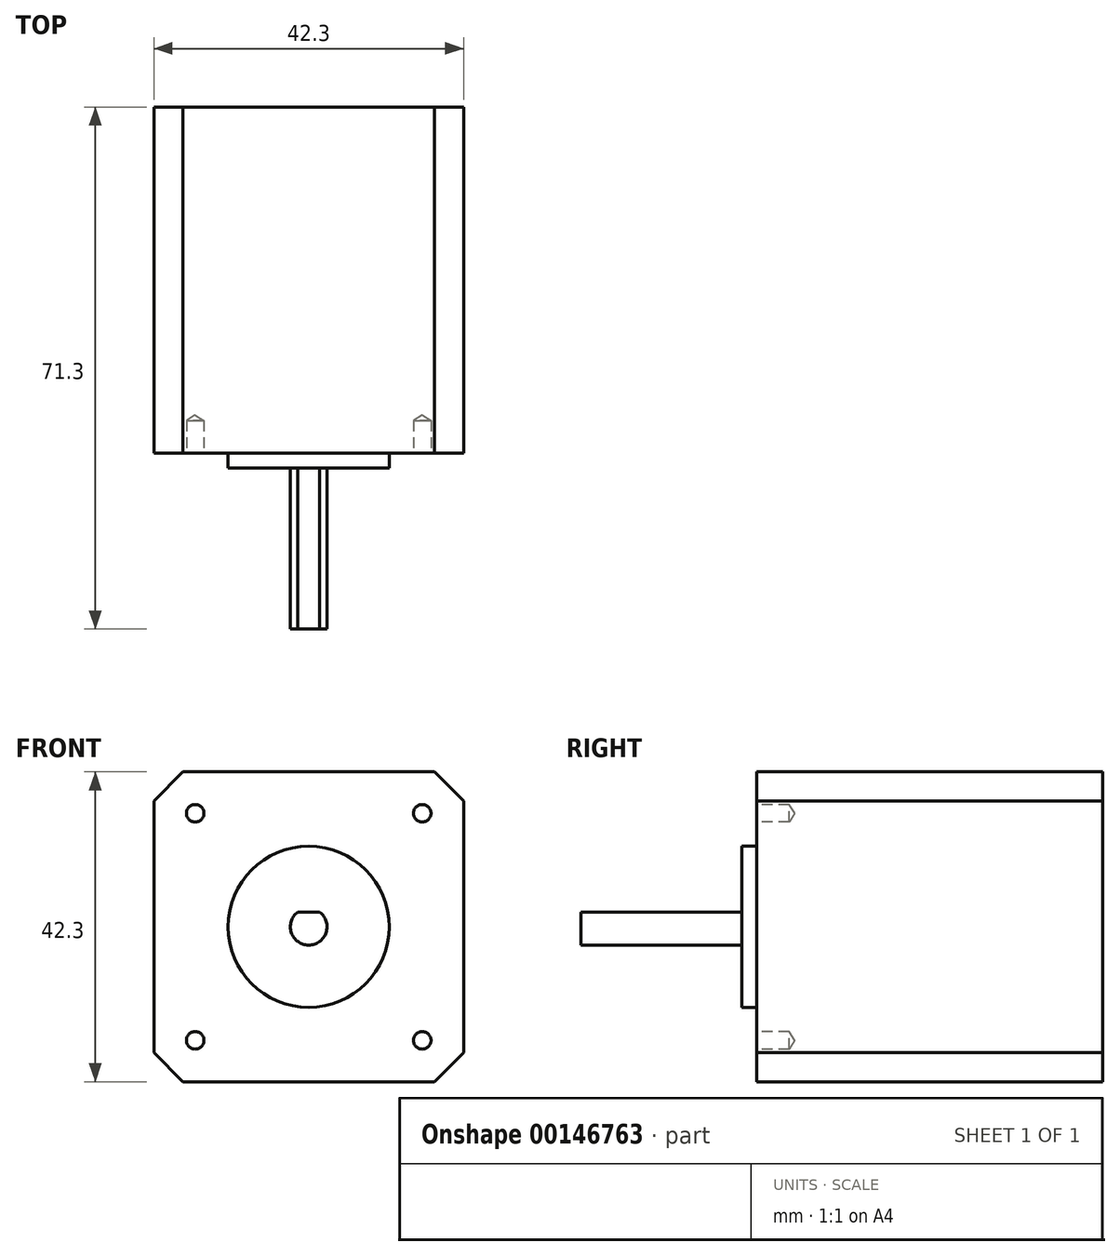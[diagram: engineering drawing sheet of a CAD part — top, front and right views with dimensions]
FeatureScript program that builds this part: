
annotation { "Feature Type Name" : "Feature", "Feature Type Description" : "" }
export const myFeature = defineFeature(function(context is Context, id is Id, definition is map)
    precondition{}
    {
        {
            var Q0;
            Q0=qCreatedBy(makeId("Front.planeOp"),FACE);
            var sketch = newSketch(context, id + "F0", { "sketchPlane" : qUnion([Q0])});
            skLineSegment(sketch, "E0.bottom", {"start": v(21.15, 21.15) * mm, "end": v(-21.15, 21.15) * mm});
            skLineSegment(sketch, "E0.top", {"start": v(21.15, -21.15) * mm, "end": v(-21.15, -21.15) * mm});
            skLineSegment(sketch, "E0.left", {"start": v(21.15, 21.15) * mm, "end": v(21.15, -21.15) * mm});
            skLineSegment(sketch, "E0.right", {"start": v(-21.15, 21.15) * mm, "end": v(-21.15, -21.15) * mm});
            skPoint(sketch, "E0.middle", {"position": v(0, 0) * mm});
            skSolve(sketch);
        }
        {
            var Q0;
            Q0=qSketchRegion(id+"F0",true);
            extrude(context, id + "F1", {"entities" : qUnion([Q0]), "oppositeDirection" : true, "depth" : 47.3 * mm});
        }
        {
            var Q0;
            Q0=qCreatedBy(makeId("Front.planeOp"),FACE);
            var sketch = newSketch(context, id + "F2", { "sketchPlane" : qUnion([Q0])});
            skCircle(sketch, "E1", {"center": v(0, 0) * mm, "radius": 11 * mm});
            skSolve(sketch);
        }
        {
            var Q0;
            Q0=qSketchRegion(id+"F2",true);
            extrude(context, id + "F3", {"entities" : qUnion([Q0]), "operationType" : NewBodyOperationType.ADD, "depth" : 2 * mm});
        }
        {
            var Q0;
            Q0=makeQuery(id+"F3.opExtrude","CAP_FACE",FACE,{"disambiguationData":[OSD([sQuery(id+"F2.wireOp",EDGE,"E1")])],"isStart":false});
            var sketch = newSketch(context, id + "F4", { "sketchPlane" : qUnion([Q0])});
            skArc(sketch, "E2", {"start": v(-1.5, 2) * mm, "mid": v(0, -2.5) * mm, "end": v(1.5, 2) * mm});
            skLineSegment(sketch, "E3", {"start": v(-1.5, 2) * mm, "end": v(1.5, 2) * mm});
            skSolve(sketch);
        }
        {
            var Q0;
            Q0=qSketchRegion(id+"F4",true);
            extrude(context, id + "F5", {"entities" : qUnion([Q0]), "operationType" : NewBodyOperationType.ADD, "depth" : 22 * mm});
        }
        {
            var Q0;
            Q0=makeQuery(id+"F1.opExtrude","CAP_FACE",FACE,{"disambiguationData":[OSD([sQuery(id+"F0.wireOp",EDGE,"E0.bottom"),sQuery(id+"F0.wireOp",EDGE,"E0.top"),sQuery(id+"F0.wireOp",EDGE,"E0.left"),sQuery(id+"F0.wireOp",EDGE,"E0.right")])],"isStart":true});
            var sketch = newSketch(context, id + "F6", { "sketchPlane" : qUnion([Q0])});
            skLineSegment(sketch, "E4.bottom", {"start": v(15.5, 15.5) * mm, "end": v(-15.5, 15.5) * mm, "construction": true});
            skLineSegment(sketch, "E4.top", {"start": v(15.5, -15.5) * mm, "end": v(-15.5, -15.5) * mm, "construction": true});
            skLineSegment(sketch, "E4.left", {"start": v(15.5, 15.5) * mm, "end": v(15.5, -15.5) * mm, "construction": true});
            skLineSegment(sketch, "E4.right", {"start": v(-15.5, 15.5) * mm, "end": v(-15.5, -15.5) * mm, "construction": true});
            skPoint(sketch, "E4.middle", {"position": v(0, 0) * mm});
            skSolve(sketch);
        }
        {
            var Q0;
            Q0=sQuery(id+"F6.wireOp",VERTEX,"E4.right.start");
            var Q1;
            Q1=sQuery(id+"F6.wireOp",VERTEX,"E4.left.start");
            var Q2;
            Q2=sQuery(id+"F6.wireOp",VERTEX,"E4.left.end");
            var Q3;
            Q3=sQuery(id+"F6.wireOp",VERTEX,"E4.right.end");
            var Q4;
            Q4=makeQuery(id+"F1.opExtrude","SWEPT_BODY",BODY,{"disambiguationData":[OSD([sQuery(id+"F0.wireOp",EDGE,"E0.bottom"),sQuery(id+"F0.wireOp",EDGE,"E0.top"),sQuery(id+"F0.wireOp",EDGE,"E0.left"),sQuery(id+"F0.wireOp",EDGE,"E0.right")])]});
            hole(context, id + "F7", {"style" : HoleStyle.SIMPLE, "endStyle" : HoleEndStyle.BLIND, "standardTappedOrClearance" : lookupTablePath({ "standard" : "ISO", "engagement" : "75%", "pitch" : "0.6 mm", "size" : "M3", "type" : "Tapped" }), "standardBlindInLast" : lookupTablePath({ "standard" : "ISO", "engagement" : "75%", "pitch" : "0.6 mm", "size" : "M3", "type" : "Tapped" }), "holeDiameter" : 2.4 * mm, "holeDepth" : 4.5 * mm, "locations" : qUnion([Q0, Q1, Q2, Q3]), "scope" : qUnion([Q4])});
        }
        {
            var Q0;
            Q0=makeQuery(id+"F1.opExtrude","SWEPT_EDGE",EDGE,{"disambiguationData":[OSD([sQuery(id+"F0.wireOp",EDGE,"E0.bottom"),sQuery(id+"F0.wireOp",EDGE,"E0.right")])]});
            var Q1;
            Q1=makeQuery(id+"F1.opExtrude","SWEPT_EDGE",EDGE,{"disambiguationData":[OSD([sQuery(id+"F0.wireOp",EDGE,"E0.top"),sQuery(id+"F0.wireOp",EDGE,"E0.right")])]});
            var Q2;
            Q2=makeQuery(id+"F1.opExtrude","SWEPT_EDGE",EDGE,{"disambiguationData":[OSD([sQuery(id+"F0.wireOp",EDGE,"E0.top"),sQuery(id+"F0.wireOp",EDGE,"E0.left")])]});
            var Q3;
            Q3=makeQuery(id+"F1.opExtrude","SWEPT_EDGE",EDGE,{"disambiguationData":[OSD([sQuery(id+"F0.wireOp",EDGE,"E0.bottom"),sQuery(id+"F0.wireOp",EDGE,"E0.left")])]});
            chamfer(context, id + "F8", {"entities" : qUnion([Q0, Q1, Q2, Q3]), "width" : 4 * mm, "tangentPropagation" : true});
        }
    });
